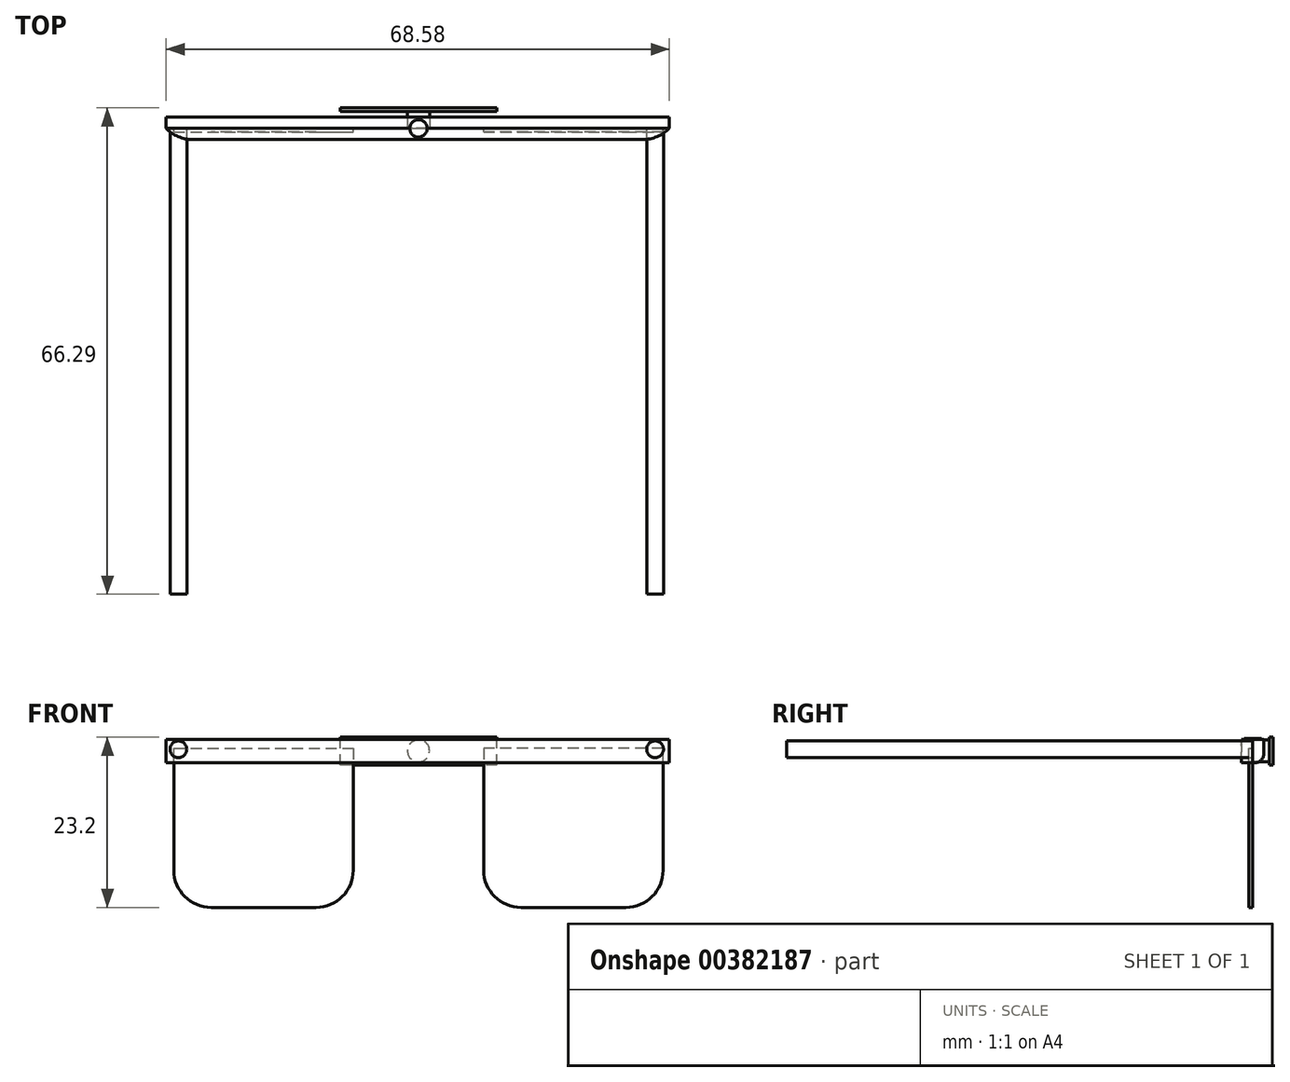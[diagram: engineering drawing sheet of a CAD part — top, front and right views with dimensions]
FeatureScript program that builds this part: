
annotation { "Feature Type Name" : "Feature", "Feature Type Description" : "" }
export const myFeature = defineFeature(function(context is Context, id is Id, definition is map)
    precondition{}
    {
        {
            var Q0;
            Q0=qCreatedBy(makeId("Front.planeOp"),FACE);
            var sketch = newSketch(context, id + "F0", { "sketchPlane" : qUnion([Q0])});
            skLineSegment(sketch, "E0", {"start": v(-33.34, 0) * mm, "end": v(-33.34, 21.67) * mm});
            skLineSegment(sketch, "E1", {"start": v(-33.34, 21.67) * mm, "end": v(-8.9, 21.67) * mm});
            skLineSegment(sketch, "E2", {"start": v(-8.9, 21.67) * mm, "end": v(-8.9, 0) * mm});
            skLineSegment(sketch, "E3", {"start": v(-8.9, 0) * mm, "end": v(-33.34, 0) * mm});
            skLineSegment(sketch, "E4.MirrorCS", {"start": v(33.34, 21.67) * mm, "end": v(8.9, 21.67) * mm});
            skLineSegment(sketch, "E5.MirrorCS", {"start": v(33.34, 0) * mm, "end": v(33.34, 21.67) * mm});
            skLineSegment(sketch, "E6.MirrorCS", {"start": v(8.9, 0) * mm, "end": v(33.34, 0) * mm});
            skLineSegment(sketch, "E7.MirrorCS", {"start": v(8.9, 21.67) * mm, "end": v(8.9, 0) * mm});
            skSolve(sketch);
        }
        {
            var Q0;
            Q0=makeQuery(id+"F0.imprint","IMPRINT",FACE,{"disambiguationData":[TD([[makeQuery(id+"F0.imprint","IMPRINT",EDGE,{"derivedFrom":sQuery(id+"F0.wireOp",EDGE,"E0")}),-1.0]])]});
            var Q1;
            Q1=makeQuery(id+"F0.imprint","IMPRINT",FACE,{"disambiguationData":[TD([[makeQuery(id+"F0.imprint","IMPRINT",EDGE,{"derivedFrom":sQuery(id+"F0.wireOp",EDGE,"E4.MirrorCS")}),1.0]])]});
            extrude(context, id + "F1", {"entities" : qUnion([Q0, Q1]), "depth" : 0.5 * mm});
        }
        {
            var Q0;
            Q0=qCreatedBy(makeId("Front.planeOp"),FACE);
            var sketch = newSketch(context, id + "F2", { "sketchPlane" : qUnion([Q0])});
            skLineSegment(sketch, "E8", {"start": v(-34.4, 19.71) * mm, "end": v(34.19, 19.71) * mm});
            skLineSegment(sketch, "E9", {"start": v(34.19, 19.71) * mm, "end": v(34.19, 22.88) * mm});
            skLineSegment(sketch, "E10", {"start": v(34.19, 22.88) * mm, "end": v(-34.4, 22.88) * mm});
            skLineSegment(sketch, "E11", {"start": v(-34.4, 22.88) * mm, "end": v(-34.4, 19.71) * mm});
            skSolve(sketch);
        }
        {
            var Q0;
            Q0=makeQuery(id+"F2.imprint","IMPRINT",FACE,{"disambiguationData":[TD([[makeQuery(id+"F2.imprint","IMPRINT",EDGE,{"derivedFrom":sQuery(id+"F2.wireOp",EDGE,"E8")}),1.0]])]});
            extrude(context, id + "F3", {"entities" : qUnion([Q0]), "depth" : 1.52 * mm});
        }
        {
            var Q0;
            Q0=makeQuery(id+"F3.opExtrude","CAP_FACE",FACE,{"disambiguationData":[OSD([sQuery(id+"F2.wireOp",EDGE,"E8"),sQuery(id+"F2.wireOp",EDGE,"E9"),sQuery(id+"F2.wireOp",EDGE,"E10"),sQuery(id+"F2.wireOp",EDGE,"E11")])],"isStart":true});
            extrude(context, id + "F4", {"entities" : qUnion([Q0]), "depth" : 1.52 * mm});
        }
        {
            var Q0;
            Q0=makeQuery(id+"F1.opExtrude","SWEPT_EDGE",EDGE,{"disambiguationData":[OSD([sQuery(id+"F0.wireOp",EDGE,"E2"),sQuery(id+"F0.wireOp",EDGE,"E3")])]});
            var Q1;
            Q1=makeQuery(id+"F1.opExtrude","SWEPT_EDGE",EDGE,{"disambiguationData":[OSD([sQuery(id+"F0.wireOp",EDGE,"E6.MirrorCS"),sQuery(id+"F0.wireOp",EDGE,"E7.MirrorCS")])]});
            var Q2;
            Q2=makeQuery(id+"F1.opExtrude","SWEPT_EDGE",EDGE,{"disambiguationData":[OSD([sQuery(id+"F0.wireOp",EDGE,"E0"),sQuery(id+"F0.wireOp",EDGE,"E3")])]});
            var Q3;
            Q3=makeQuery(id+"F1.opExtrude","SWEPT_EDGE",EDGE,{"disambiguationData":[OSD([sQuery(id+"F0.wireOp",EDGE,"E5.MirrorCS"),sQuery(id+"F0.wireOp",EDGE,"E6.MirrorCS")])]});
            fillet(context, id + "F5", {"entities" : qUnion([Q0, Q1, Q2, Q3]), "radius" : 5.08 * mm, "tangentPropagation" : true, "allowEdgeOverflow" : false});
        }
        {
            var Q0;
            Q0=qCreatedBy(makeId("Front.planeOp"),FACE);
            var sketch = newSketch(context, id + "F6", { "sketchPlane" : qUnion([Q0])});
            skCircle(sketch, "E12", {"center": v(32.25, 21.56) * mm, "radius": 1.14 * mm});
            skCircle(sketch, "E13", {"center": v(-32.73, 21.56) * mm, "radius": 1.14 * mm});
            skSolve(sketch);
        }
        {
            var Q0;
            Q0 = qSketchRegion(id + "F6", true);
            extrude(context, id + "F7", {"entities" : qUnion([Q0]), "depth" : 63.5 * mm});
        }
        {
            var Q0;
            Q0=makeQuery(id+"F4.opExtrude","CAP_EDGE",EDGE,{"disambiguationData":[OSD([sQuery(id+"F2.wireOp",EDGE,"E8")])],"isStart":false});
            fillet(context, id + "F8", {"entities" : qUnion([Q0]), "radius" : 1.27 * mm, "tangentPropagation" : true, "allowEdgeOverflow" : false});
        }
        {
            var Q0;
            Q0=makeQuery(id+"F3.opExtrude","CAP_EDGE",EDGE,{"disambiguationData":[OSD([sQuery(id+"F2.wireOp",EDGE,"E9")])],"isStart":false});
            var Q1;
            Q1=makeQuery(id+"F3.opExtrude","CAP_EDGE",EDGE,{"disambiguationData":[OSD([sQuery(id+"F2.wireOp",EDGE,"E11")])],"isStart":false});
            fillet(context, id + "F9", {"entities" : qUnion([Q0, Q1]), "radius" : 5.08 * mm, "tangentPropagation" : true, "allowEdgeOverflow" : false});
        }
        {
            var Q0;
            Q0=qCreatedBy(makeId("Front.planeOp"),FACE);
            var sketch = newSketch(context, id + "F10", { "sketchPlane" : qUnion([Q0])});
            skCircle(sketch, "E14", {"center": v(0, 21.34) * mm, "radius": 1.5 * mm});
            skSolve(sketch);
        }
        {
            var Q0;
            Q0 = qSketchRegion(id + "F10", true);
            extrude(context, id + "F11", {"entities" : qUnion([Q0]), "oppositeDirection" : true, "depth" : 2.3 * mm});
        }
        {
            var Q0;
            Q0=makeQuery(id+"F11.opExtrude","CAP_FACE",FACE,{"disambiguationData":[OSD([sQuery(id+"F10.wireOp",EDGE,"E14")])],"isStart":false});
            var sketch = newSketch(context, id + "F12", { "sketchPlane" : qUnion([Q0])});
            skLineSegment(sketch, "E15.bottom", {"start": v(-10.7, 19.4) * mm, "end": v(10.65, 19.4) * mm});
            skLineSegment(sketch, "E15.top", {"start": v(-10.7, 23.2) * mm, "end": v(10.65, 23.2) * mm});
            skLineSegment(sketch, "E15.left", {"start": v(-10.7, 19.4) * mm, "end": v(-10.7, 23.2) * mm});
            skLineSegment(sketch, "E15.right", {"start": v(10.65, 19.4) * mm, "end": v(10.65, 23.2) * mm});
            skSolve(sketch);
        }
        {
            var Q0;
            Q0=makeQuery(id+"F12.imprint","IMPRINT",FACE,{"disambiguationData":[TD([[makeQuery(id+"F12.imprint","IMPRINT",EDGE,{"derivedFrom":sQuery(id+"F12.wireOp",EDGE,"E15.bottom")}),1.0]])]});
            var Q1;
            Q1=makeQuery(id+"F12.imprint","IMPRINT",FACE,{"disambiguationData":[TD([[makeQuery(id+"F12.imprint","IMPRINT",EDGE,{"derivedFrom":makeQuery(id+"F11.opExtrude","CAP_EDGE",EDGE,{"disambiguationData":[OSD([sQuery(id+"F10.wireOp",EDGE,"E14")])],"isStart":false})}),-1.0]])]});
            extrude(context, id + "F13", {"entities" : qUnion([Q0, Q1]), "depth" : 0.5 * mm});
        }
        {
            var Q0;
            Q0=makeQuery(id+"F3.opExtrude","SWEPT_FACE",FACE,{"disambiguationData":[OSD([sQuery(id+"F2.wireOp",EDGE,"E10")])]});
            var sketch = newSketch(context, id + "F14", { "sketchPlane" : qUnion([Q0])});
            skCircle(sketch, "E16", {"center": v(0, 0) * mm, "radius": 1.19 * mm});
            skSolve(sketch);
        }
        {
            var Q0;
            {var subQ0=sQuery(id+"F14.wireOp",EDGE,"E16");var subQ1=makeQuery(id+"F3.opExtrude","CAP_EDGE",EDGE,{"disambiguationData":[OSD([sQuery(id+"F2.wireOp",EDGE,"E10")])],"isStart":true});var subQ2=makeQuery(id+"F14.imprint","INTERSECT",VERTEX,{"disambiguationData":[OD(0.0)],"derivedFrom":[subQ1,subQ0]});Q0=makeQuery(id+"F14.imprint","IMPRINT",FACE,{"disambiguationData":[TD([[makeQuery(id+"F14.imprint","IMPRINT",EDGE,{"disambiguationData":[TD([[subQ2,-1.0]])],"derivedFrom":subQ0}),1.0]])]});}
            var Q1;
            {var subQ0=sQuery(id+"F14.wireOp",EDGE,"E16");var subQ1=makeQuery(id+"F3.opExtrude","CAP_EDGE",EDGE,{"disambiguationData":[OSD([sQuery(id+"F2.wireOp",EDGE,"E10")])],"isStart":true});var subQ2=makeQuery(id+"F14.imprint","INTERSECT",VERTEX,{"disambiguationData":[OD(0.0)],"derivedFrom":[subQ1,subQ0]});Q1=makeQuery(id+"F14.imprint","IMPRINT",FACE,{"disambiguationData":[TD([[makeQuery(id+"F14.imprint","IMPRINT",EDGE,{"disambiguationData":[TD([[subQ2,1.0]])],"derivedFrom":subQ0}),1.0]])]});}
            extrude(context, id + "F15", {"entities" : qUnion([Q0, Q1]), "depth" : 0.13 * mm});
        }
    });
